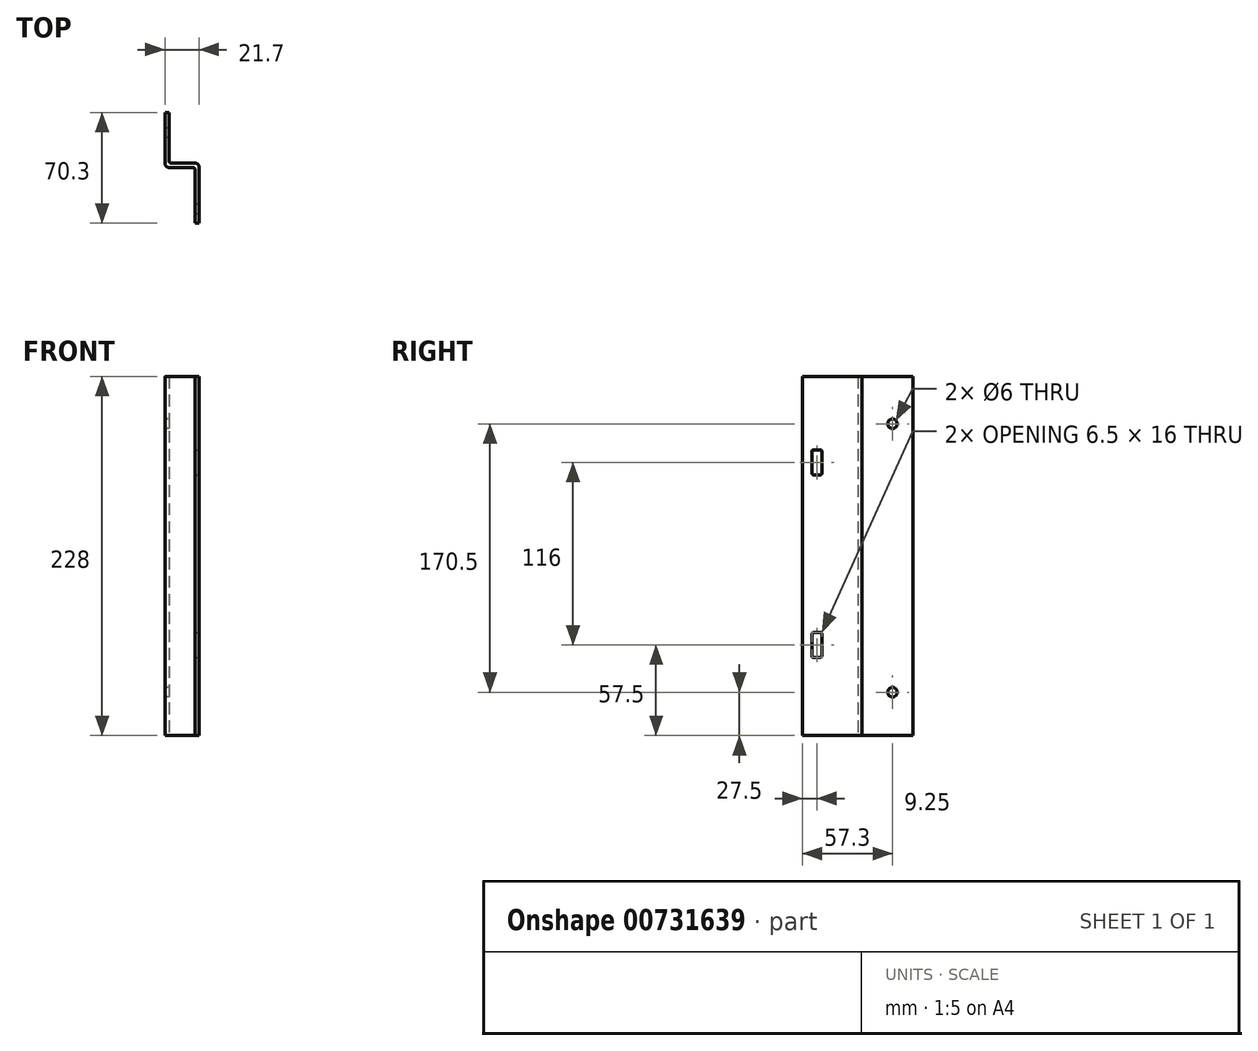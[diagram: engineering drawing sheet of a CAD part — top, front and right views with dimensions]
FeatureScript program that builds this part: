
annotation { "Feature Type Name" : "Feature", "Feature Type Description" : "" }
export const myFeature = defineFeature(function(context is Context, id is Id, definition is map)
    precondition{}
    {
        {
            var Q0;
            Q0=qCreatedBy(makeId("Top.planeOp"),FACE);
            var sketch = newSketch(context, id + "F0", { "sketchPlane" : qUnion([Q0])});
            skLineSegment(sketch, "E0", {"start": v(0, 0) * mm, "end": v(0, -32.5) * mm});
            skLineSegment(sketch, "E1", {"start": v(2.5, -35) * mm, "end": v(17.75, -35) * mm});
            skLineSegment(sketch, "E2", {"start": v(19, -36.25) * mm, "end": v(19, -70.3) * mm});
            skLineSegment(sketch, "E3", {"start": v(19, -70.3) * mm, "end": v(21.7, -70.3) * mm});
            skLineSegment(sketch, "E4", {"start": v(21.7, -70.3) * mm, "end": v(21.7, -34.8) * mm});
            skLineSegment(sketch, "E5", {"start": v(19.2, -32.3) * mm, "end": v(3.95, -32.3) * mm});
            skLineSegment(sketch, "E6", {"start": v(2.7, -31.05) * mm, "end": v(2.7, 0) * mm});
            skLineSegment(sketch, "E7", {"start": v(2.7, 0) * mm, "end": v(0, 0) * mm});
            skPoint(sketch, "E8.visualSharp", {"position": v(21.7, -32.3) * mm});
            skArc(sketch, "E8.filletArc", {"start": v(21.7, -34.8) * mm, "mid": v(20.97, -33.03) * mm, "end": v(19.2, -32.3) * mm});
            skPoint(sketch, "E9.visualSharp", {"position": v(0, -35) * mm});
            skArc(sketch, "E9.filletArc", {"start": v(0, -32.5) * mm, "mid": v(0.73, -34.27) * mm, "end": v(2.5, -35) * mm});
            skPoint(sketch, "E10.visualSharp", {"position": v(2.7, -32.3) * mm});
            skArc(sketch, "E10.filletArc", {"start": v(2.7, -31.05) * mm, "mid": v(3.07, -31.93) * mm, "end": v(3.95, -32.3) * mm});
            skPoint(sketch, "E11.visualSharp", {"position": v(19, -35) * mm});
            skArc(sketch, "E11.filletArc", {"start": v(19, -36.25) * mm, "mid": v(18.63, -35.37) * mm, "end": v(17.75, -35) * mm});
            skSolve(sketch);
        }
        {
            var Q0;
            Q0=makeQuery(id+"F0.imprint","IMPRINT",FACE,{"disambiguationData":[TD([[makeQuery(id+"F0.imprint","IMPRINT",EDGE,{"derivedFrom":sQuery(id+"F0.wireOp",EDGE,"E0")}),1.0]])]});
            extrude(context, id + "F1", {"entities" : qUnion([Q0]), "depth" : 228 * mm, "offsetDistance" : 25 * mm});
        }
        {
            var Q0;
            Q0=makeQuery(id+"F1.opExtrude","SWEPT_FACE",FACE,{"disambiguationData":[OSD([sQuery(id+"F0.wireOp",EDGE,"E0")])]});
            var sketch = newSketch(context, id + "F2", { "sketchPlane" : qUnion([Q0])});
            skCircle(sketch, "E12", {"center": v(13, 198) * mm, "radius": 3 * mm});
            skCircle(sketch, "E13", {"center": v(13, 27.5) * mm, "radius": 3 * mm});
            skSolve(sketch);
        }
        {
            var Q0;
            Q0 = qSketchRegion(id + "F2", true);
            extrude(context, id + "F3", {"entities" : qUnion([Q0]), "operationType" : NewBodyOperationType.REMOVE, "oppositeDirection" : true, "depth" : 2.7 * mm, "offsetDistance" : 25 * mm});
        }
        {
            var Q0;
            Q0=makeQuery(id+"F1.opExtrude","SWEPT_FACE",FACE,{"disambiguationData":[OSD([sQuery(id+"F0.wireOp",EDGE,"E4")])]});
            var sketch = newSketch(context, id + "F4", { "sketchPlane" : qUnion([Q0])});
            skLineSegment(sketch, "E14.bottom", {"start": v(-59.05, 65.5) * mm, "end": v(-63.05, 65.5) * mm});
            skLineSegment(sketch, "E14.top", {"start": v(-59.05, 49.5) * mm, "end": v(-63.05, 49.5) * mm});
            skLineSegment(sketch, "E14.left", {"start": v(-57.8, 64.25) * mm, "end": v(-57.8, 50.75) * mm});
            skLineSegment(sketch, "E14.right", {"start": v(-64.3, 64.25) * mm, "end": v(-64.3, 50.75) * mm});
            skLineSegment(sketch, "E15.bottom", {"start": v(-59.05, 181.5) * mm, "end": v(-63.05, 181.5) * mm});
            skLineSegment(sketch, "E15.top", {"start": v(-59.05, 165.5) * mm, "end": v(-63.05, 165.5) * mm});
            skLineSegment(sketch, "E15.left", {"start": v(-57.8, 180.25) * mm, "end": v(-57.8, 166.75) * mm});
            skLineSegment(sketch, "E15.right", {"start": v(-64.3, 180.25) * mm, "end": v(-64.3, 166.75) * mm});
            skPoint(sketch, "E16.visualSharp", {"position": v(-57.8, 181.5) * mm});
            skArc(sketch, "E16.filletArc", {"start": v(-57.8, 180.25) * mm, "mid": v(-58.17, 181.13) * mm, "end": v(-59.05, 181.5) * mm});
            skPoint(sketch, "E17.visualSharp", {"position": v(-64.3, 181.5) * mm});
            skArc(sketch, "E17.filletArc", {"start": v(-63.05, 181.5) * mm, "mid": v(-63.93, 181.13) * mm, "end": v(-64.3, 180.25) * mm});
            skPoint(sketch, "E18.visualSharp", {"position": v(-57.8, 165.5) * mm});
            skArc(sketch, "E18.filletArc", {"start": v(-59.05, 165.5) * mm, "mid": v(-58.17, 165.87) * mm, "end": v(-57.8, 166.75) * mm});
            skPoint(sketch, "E19.visualSharp", {"position": v(-64.3, 165.5) * mm});
            skArc(sketch, "E19.filletArc", {"start": v(-64.3, 166.75) * mm, "mid": v(-63.93, 165.87) * mm, "end": v(-63.05, 165.5) * mm});
            skPoint(sketch, "E20.visualSharp", {"position": v(-57.8, 65.5) * mm});
            skArc(sketch, "E20.filletArc", {"start": v(-57.8, 64.25) * mm, "mid": v(-58.17, 65.13) * mm, "end": v(-59.05, 65.5) * mm});
            skPoint(sketch, "E21.visualSharp", {"position": v(-64.3, 65.5) * mm});
            skArc(sketch, "E21.filletArc", {"start": v(-63.05, 65.5) * mm, "mid": v(-63.93, 65.13) * mm, "end": v(-64.3, 64.25) * mm});
            skPoint(sketch, "E22.visualSharp", {"position": v(-64.3, 49.5) * mm});
            skArc(sketch, "E22.filletArc", {"start": v(-64.3, 50.75) * mm, "mid": v(-63.93, 49.87) * mm, "end": v(-63.05, 49.5) * mm});
            skPoint(sketch, "E23.visualSharp", {"position": v(-57.8, 49.5) * mm});
            skArc(sketch, "E23.filletArc", {"start": v(-59.05, 49.5) * mm, "mid": v(-58.17, 49.87) * mm, "end": v(-57.8, 50.75) * mm});
            skSolve(sketch);
        }
        {
            var Q0;
            Q0 = qSketchRegion(id + "F4", true);
            extrude(context, id + "F5", {"entities" : qUnion([Q0]), "operationType" : NewBodyOperationType.REMOVE, "oppositeDirection" : true, "depth" : 2.7 * mm, "offsetDistance" : 25 * mm});
        }
    });
